# Revit family: Ceileo T
name_source: partatom
category: Mechanical Equipment
units: mm (PartAtom-declared; Revit-internal decimal feet)

## family parameters
Always vertical = Yes
Classification = None
Cut with Voids When Loaded = No
Part Type = Normal
Room Calculation Point = No
Round Connector Dimension = Use Diameter
Shared = No
Work Plane-Based = No

## types (6) — shared parameters
00_20_Manufacturer = Blauberg
00_20_Name = Centrifugal ceiling extract fan
A = 330 mm  [stored 1.08268 ft]
Amperage = 0 A
B = 258 mm  [stored 0.846457 ft]
B1 = 158 mm
C = 260 mm  [stored 0.853018 ft]
Casing Material = Plastic, opaque, white
Description = For round channels
E = 395 mm  [stored 1.29593 ft]
Frequency = 50 Hz
H = 188 mm  [stored 0.616798 ft]
H1 = 88 mm  [stored 0.288714 ft]
Height = 206 mm  [stored 0.675853 ft]
Length = 395 mm  [stored 1.29593 ft]
Load Classification = HVAC
Maintenance zone material = <By Category>
Manufacturer = Blauberg
Number of Fase = 1
URL = https://blaubergventilatoren.de
Voltage = 230 V
Width = 260 mm  [stored 0.853018 ft]
b = 129 mm  [stored 0.423228 ft]
d = 98 mm  [stored 0.321522 ft]
h = 18 mm  [stored 0.0590551 ft]
r = 49 mm  [stored 0.160761 ft]
zero-valued in all types: Default Elevation

## per-type parameters (varying)
| type | Apparent Load | B2 | D | Diameter | Dy | L1 | Maximum Air Flow | Power | R | Sound pressure level at 3 m distance | Weight | l2 | l3 |
| Ceileo 200 | 30 W | 45 mm  [stored 0.147638 ft] | 148 mm  [stored 0.485564 ft] | 148 mm  [stored 0.485564 ft] | 143 mm | 100 mm  [stored 0.328084 ft] | 210.0 m³/h | 29 W | 74 mm  [stored 0.242782 ft] | 27 dBA | 5.30 kg | 45 mm  [stored 0.147638 ft] | 70 mm  [stored 0.229659 ft] |
| Ceileo 250 | 41 W | 45 mm  [stored 0.147638 ft] | 148 mm  [stored 0.485564 ft] | 148 mm  [stored 0.485564 ft] | 143 mm | 100 mm  [stored 0.328084 ft] | 260.0 m³/h | 39 W | 74 mm  [stored 0.242782 ft] | 29 dBA | 5.30 kg | 45 mm  [stored 0.147638 ft] | 70 mm  [stored 0.229659 ft] |
| Ceileo 300 | 51 W | 0 mm  [stored 0 ft] | 149 mm  [stored 0.488845 ft] | 149 mm  [stored 0.488845 ft] | 144 mm  [stored 0.472441 ft] | 50 mm  [stored 0.164042 ft] | 300.0 m³/h | 49 W | 75 mm | 31 dBA | 5.10 kg | 20 mm  [stored 0.0656168 ft] | 35 mm  [stored 0.114829 ft] |
| Ceileo 200 T | 30 W | 45 mm  [stored 0.147638 ft] | 148 mm  [stored 0.485564 ft] | 148 mm  [stored 0.485564 ft] | 143 mm | 100 mm  [stored 0.328084 ft] | 210.0 m³/h | 29 W | 74 mm  [stored 0.242782 ft] | 27 dBA | 5.30 kg | 45 mm  [stored 0.147638 ft] | 70 mm  [stored 0.229659 ft] |
| Ceileo 250 T | 41 W | 45 mm  [stored 0.147638 ft] | 148 mm  [stored 0.485564 ft] | 148 mm  [stored 0.485564 ft] | 143 mm | 100 mm  [stored 0.328084 ft] | 260.0 m³/h | 39 W | 74 mm  [stored 0.242782 ft] | 29 dBA | 5.30 kg | 45 mm  [stored 0.147638 ft] | 70 mm  [stored 0.229659 ft] |
| Ceileo 300 T | 51 W | 0 mm  [stored 0 ft] | 149 mm  [stored 0.488845 ft] | 149 mm  [stored 0.488845 ft] | 144 mm  [stored 0.472441 ft] | 50 mm  [stored 0.164042 ft] | 300.0 m³/h | 49 W | 75 mm | 31 dBA | 5.10 kg | 20 mm  [stored 0.0656168 ft] | 35 mm  [stored 0.114829 ft] |

note: column(s) folded — value = type name in every type: 00_20_Type

note: [stored X ft] marks values corroborated as IEEE doubles in the binary element streams (Revit-internal decimal feet)
